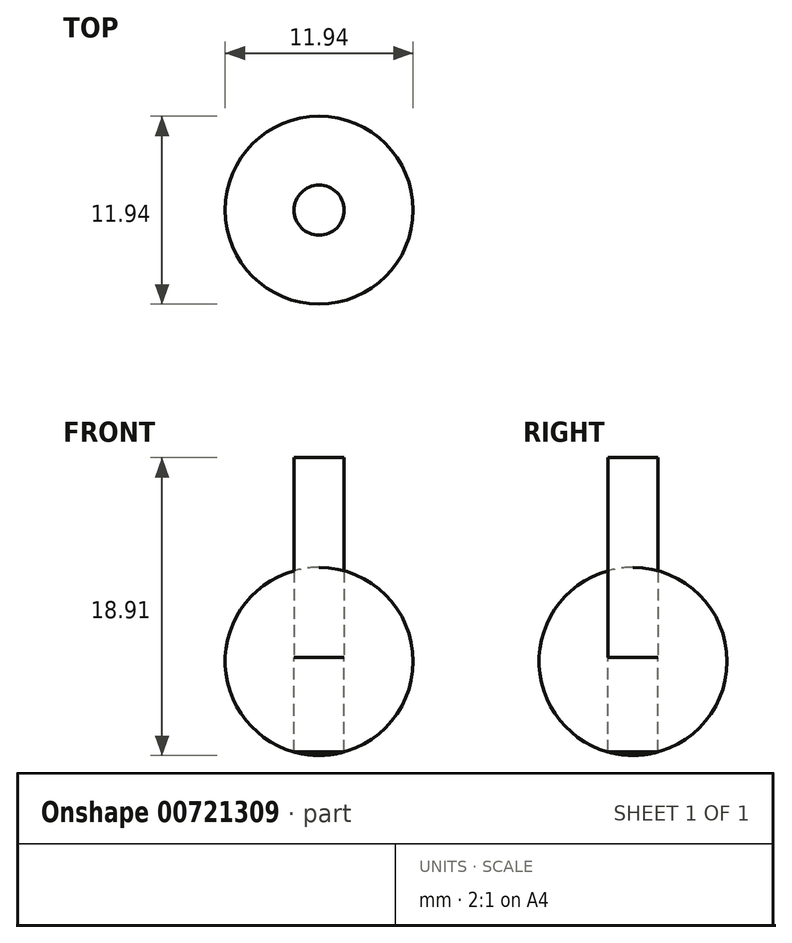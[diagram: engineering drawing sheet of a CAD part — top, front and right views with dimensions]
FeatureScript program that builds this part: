
annotation { "Feature Type Name" : "Feature", "Feature Type Description" : "" }
export const myFeature = defineFeature(function(context is Context, id is Id, definition is map)
    precondition{}
    {
        {
            assignVariable(context, id + "F0", {"name" : "balldiameter", "anyValue" : .47});
        }
        {
            assignVariable(context, id + "F1", {"name" : "ballradius", "anyValue" : (getVariable(context, 'balldiameter')) * (.5)});
        }
        {
            var Q0;
            Q0=qCreatedBy(makeId("Front.planeOp"),FACE);
            var sketch = newSketch(context, id + "F2", { "sketchPlane" : qUnion([Q0])});
            skLineSegment(sketch, "E0", {"start": v(0, 5.97) * mm, "end": v(0, -5.97) * mm});
            skArc(sketch, "E1", {"start": v(0, -5.97) * mm, "mid": v(5.97, 0) * mm, "end": v(0, 5.97) * mm});
            skSolve(sketch);
        }
        {
            var Q0;
            Q0=makeQuery(id+"F2.imprint","IMPRINT",FACE,{"disambiguationData":[TD([[makeQuery(id+"F2.imprint","IMPRINT",EDGE,{"derivedFrom":sQuery(id+"F2.wireOp",EDGE,"E0")}),1.0]])]});
            var Q1;
            Q1=sQuery(id+"F2.wireOp",EDGE,"E0");
            revolve(context, id + "F3", {"surfaceOperationType" : NewSurfaceOperationType.NEW, "entities" : qUnion([Q0]), "axis" : qUnion([Q1]), "revolveType" : RevolveType.FULL});
        }
        {
            var Q0;
            Q0=qCreatedBy(makeId("Top.planeOp"),FACE);
            cPlane(context, id + "F4", {"entities" : qUnion([Q0]), "cplaneType" : CPlaneType.OFFSET, "offset" : (getVariable(context, 'ballradius')) * mm, "width" : 152.4 * mm, "height" : 152.4 * mm});
        }
        {
            var Q0;
            Q0=qCreatedBy(id+"F4.planeOp",FACE);
            var sketch = newSketch(context, id + "F5", { "sketchPlane" : qUnion([Q0])});
            skCircle(sketch, "E2", {"center": v(0, 0) * mm, "radius": 1.59 * mm});
            skSolve(sketch);
        }
        {
            var Q0;
            Q0 = qSketchRegion(id + "F5", true);
            extrude(context, id + "F6", {"entities" : qUnion([Q0]), "depth" : 12.7 * mm, "offsetDistance" : 25.4 * mm});
        }
        {
            var Q0;
            Q0=makeQuery(id+"F6.opExtrude","CAP_FACE",FACE,{"disambiguationData":[OSD([sQuery(id+"F5.wireOp",EDGE,"E2")])],"isStart":true});
            var Q1;
            Q1=makeQuery(id+"F3.opRevolve","SWEPT_FACE",FACE,{"disambiguationData":[OSD([sQuery(id+"F2.wireOp",EDGE,"E1")])]});
            extrude(context, id + "F7", {"entities" : qUnion([Q0]), "endBound" : BoundingType.UP_TO_SURFACE, "depth" : 25.4 * mm, "endBoundEntityFace" : qUnion([Q1]), "offsetDistance" : 25.4 * mm});
        }
    });
